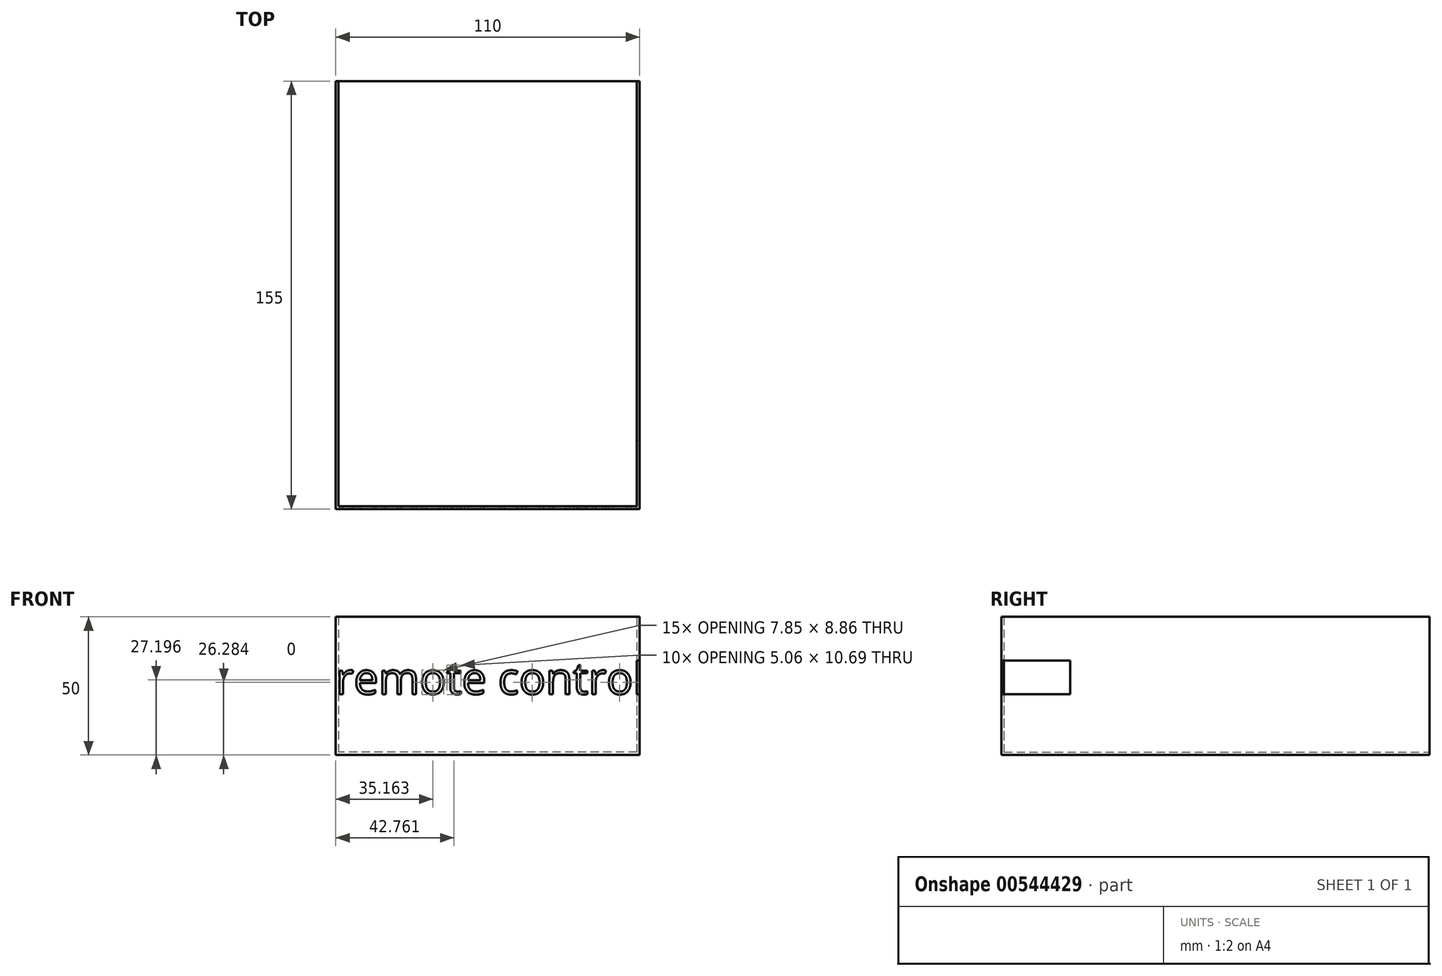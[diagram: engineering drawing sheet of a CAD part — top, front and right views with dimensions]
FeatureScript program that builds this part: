
annotation { "Feature Type Name" : "Feature", "Feature Type Description" : "" }
export const myFeature = defineFeature(function(context is Context, id is Id, definition is map)
    precondition{}
    {
        {
            var Q0;
            Q0=qCreatedBy(makeId("Top.planeOp"),FACE);
            var sketch = newSketch(context, id + "F0", { "sketchPlane" : qUnion([Q0])});
            skLineSegment(sketch, "E0.bottom", {"start": v(-55, -90) * mm, "end": v(55, -90) * mm});
            skLineSegment(sketch, "E0.top", {"start": v(-55, 90) * mm, "end": v(55, 90) * mm});
            skLineSegment(sketch, "E0.left", {"start": v(-55, -90) * mm, "end": v(-55, 90) * mm});
            skLineSegment(sketch, "E0.right", {"start": v(55, -90) * mm, "end": v(55, 90) * mm});
            skPoint(sketch, "E0.middle", {"position": v(0, 0) * mm});
            skSolve(sketch);
        }
        {
            var Q0;
            Q0 = qSketchRegion(id + "F0", true);
            extrude(context, id + "F1", {"entities" : qUnion([Q0]), "depth" : 50 * mm, "offsetDistance" : 25 * mm});
        }
        {
            var Q0;
            Q0=makeQuery(id+"F1.opExtrude","CAP_FACE",FACE,{"disambiguationData":[OSD([sQuery(id+"F0.wireOp",EDGE,"E0.bottom"),sQuery(id+"F0.wireOp",EDGE,"E0.top"),sQuery(id+"F0.wireOp",EDGE,"E0.left"),sQuery(id+"F0.wireOp",EDGE,"E0.right")])],"isStart":false});
            shell(context, id + "F2", {"entities" : qUnion([Q0]), "thickness" : 1 * mm});
        }
        {
            var Q0;
            Q0=makeQuery(id+"F1.opExtrude","SWEPT_FACE",FACE,{"disambiguationData":[OSD([sQuery(id+"F0.wireOp",EDGE,"E0.bottom")])]});
            var sketch = newSketch(context, id + "F3", { "sketchPlane" : qUnion([Q0])});
            skText(sketch, "E1", { "text": "remote control", "fontName": "OpenSans-Regular.ttf"});
            const initialGuessF3  = {"E1": [-0.055, 0.02201, 1, 0, 0.0115]};
            skSetInitialGuess(sketch, initialGuessF3);
            skSolve(sketch);
        }
        {
            var Q0;
            Q0 = qSketchRegion(id + "F3", true);
            extrude(context, id + "F4", {"entities" : qUnion([Q0]), "operationType" : NewBodyOperationType.REMOVE, "oppositeDirection" : true, "depth" : 25 * mm, "offsetDistance" : 25 * mm});
        }
        {
            var Q0;
            Q0=makeQuery(id+"F1.opExtrude","SWEPT_FACE",FACE,{"disambiguationData":[OSD([sQuery(id+"F0.wireOp",EDGE,"E0.top")])]});
            extrude(context, id + "F5", {"entities" : qUnion([Q0]), "operationType" : NewBodyOperationType.REMOVE, "oppositeDirection" : true, "depth" : 25 * mm, "offsetDistance" : 25 * mm});
        }
    });
